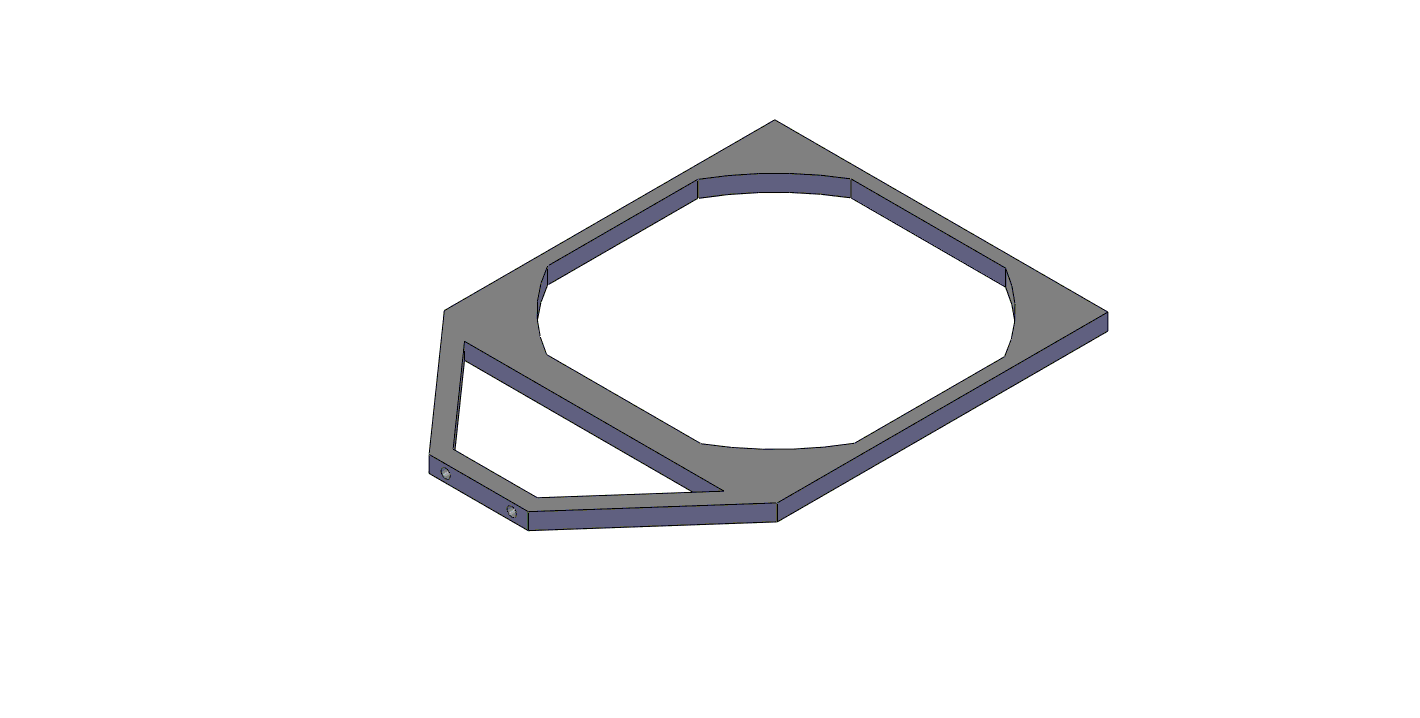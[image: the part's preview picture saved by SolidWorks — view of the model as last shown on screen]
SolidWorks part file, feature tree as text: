
SOLIDWORKS PART (.sldprt)
format: sldprt  version: not decoded by parser v0  size: 219,648 bytes
history: native  units: mm
features: sketch x4, extrude x2, material x1, hole x1 (+11 scaffold rows collapsed)
feature tree (19):
  scaffold x11  (default folders/planes/origin — collapsed)
  material  "6061-T6 (SS)"
  sketch  "Sketch2"  dims[c1.D8=120.0mm c1.D9=80.0mm c1.D12=80.0mm c1.D1=136.525mm c1.D2=120.65mm c2.D1=128.0mm c2.D2=7.0mm c2.D3=28.0mm c2.D4=5.0mm c2.D5=105.0mm c2.D6=39.0mm c2.D7=105.0mm c2.D10=15.0mm c2.D11=15.0mm c2.D13=5.0mm c2.D14=5.0mm]
  extrude  "Boss-Extrude1"  Depth=6.35mm
  sketch  "Sketch3"  dims[c1.D1=38.1mm c1.D2=50.8mm c1.D3=25.4mm c1.D4=64.5mm c2.D3=6.35mm]
  extrude  "Boss-Extrude2"  Depth=6.35mm
  hole  "#6-32 Tapped Hole1"  Diameter=2.7051mm Depth=9.398mm
  sketch  "Sketch5"  dims[D1=12.7mm D2=12.7mm]
  sketch  "Sketch4"  dims[hole-wizard template sketch: 34 standard entries collapsed; hole parameters above]
decode coverage: 7 of 7 modeling features carry decoded parameters
note: ~ marks probable driven/reference dimensions
note: suppression state not decoded; provenance and decode notes live in map.json
